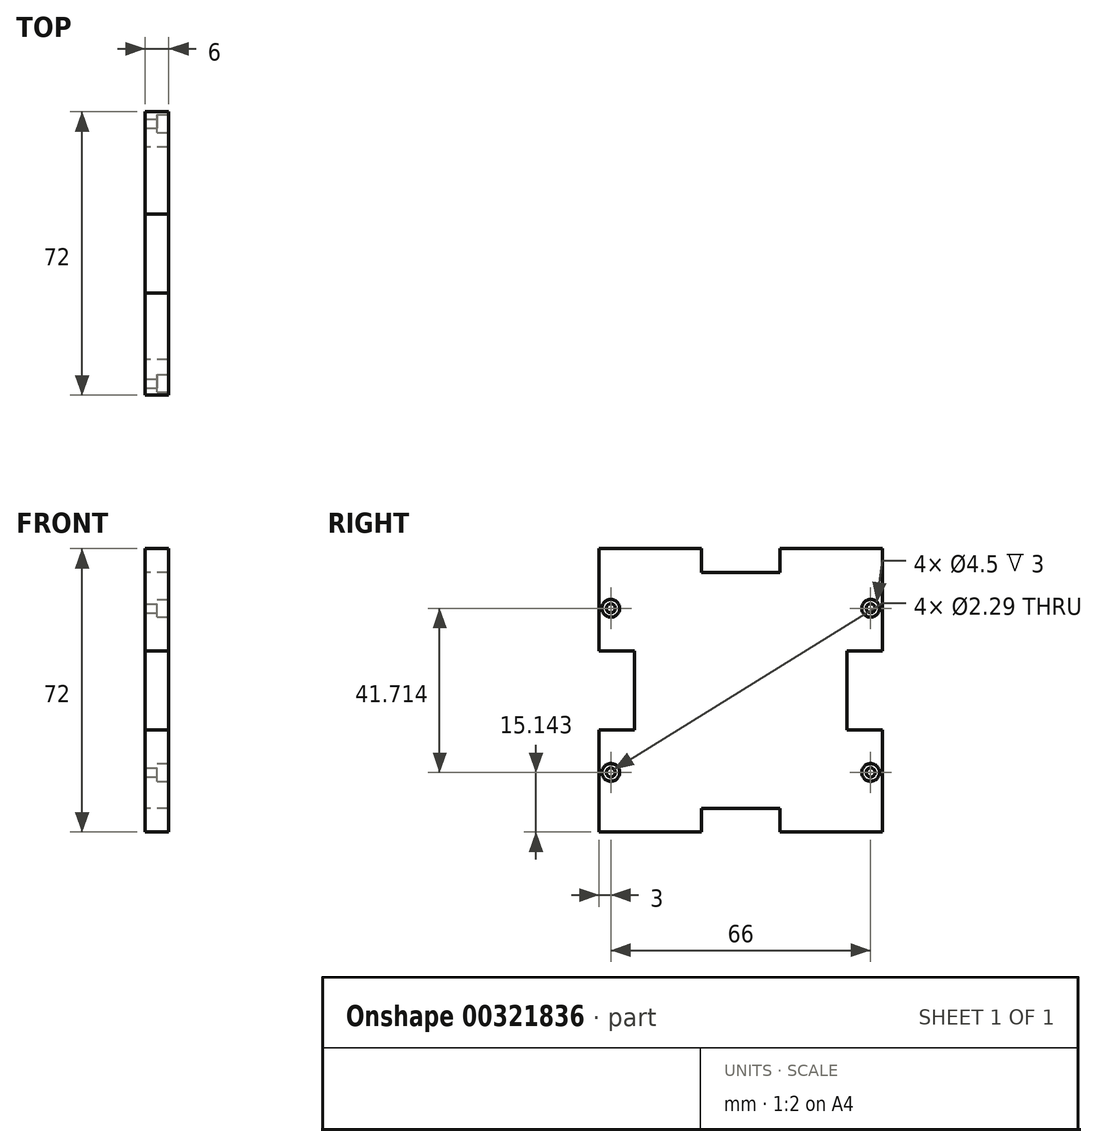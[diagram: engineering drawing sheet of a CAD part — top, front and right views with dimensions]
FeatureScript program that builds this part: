
annotation { "Feature Type Name" : "Feature", "Feature Type Description" : "" }
export const myFeature = defineFeature(function(context is Context, id is Id, definition is map)
    precondition{}
    {
        {
            var Q0;
            Q0=qCreatedBy(makeId("Right.planeOp"),FACE);
            var sketch = newSketch(context, id + "F0", { "sketchPlane" : qUnion([Q0])});
            skLineSegment(sketch, "E0.bottom", {"start": v(-36, -36) * mm, "end": v(36, -36) * mm});
            skLineSegment(sketch, "E0.top", {"start": v(-36, 36) * mm, "end": v(36, 36) * mm});
            skLineSegment(sketch, "E0.left", {"start": v(-36, -36) * mm, "end": v(-36, 36) * mm});
            skLineSegment(sketch, "E0.right", {"start": v(36, -36) * mm, "end": v(36, 36) * mm});
            skPoint(sketch, "E0.middle", {"position": v(0, 0) * mm});
            skLineSegment(sketch, "E1", {"start": v(0, 36) * mm, "end": v(0, -36) * mm, "construction": true});
            skLineSegment(sketch, "E2", {"start": v(-36, 0) * mm, "end": v(36, 0) * mm, "construction": true});
            skLineSegment(sketch, "E3", {"start": v(-36, 10) * mm, "end": v(-27, 10) * mm});
            skLineSegment(sketch, "E4", {"start": v(-27, 10) * mm, "end": v(-27, -10) * mm});
            skLineSegment(sketch, "E5", {"start": v(-27, -10) * mm, "end": v(-36, -10) * mm});
            skLineSegment(sketch, "E6.MirrorCS", {"start": v(36, 10) * mm, "end": v(27, 10) * mm});
            skLineSegment(sketch, "E7.MirrorCS", {"start": v(27, 10) * mm, "end": v(27, -10) * mm});
            skLineSegment(sketch, "E8.MirrorCS", {"start": v(27, -10) * mm, "end": v(36, -10) * mm});
            skLineSegment(sketch, "E9", {"start": v(-10, 36) * mm, "end": v(-10, 30) * mm});
            skLineSegment(sketch, "E10", {"start": v(-10, 30) * mm, "end": v(10, 30) * mm});
            skLineSegment(sketch, "E11", {"start": v(10, 30) * mm, "end": v(10, 36) * mm});
            skLineSegment(sketch, "E12.MirrorCS", {"start": v(10, -30) * mm, "end": v(10, -36) * mm});
            skLineSegment(sketch, "E13.MirrorCS", {"start": v(-10, -36) * mm, "end": v(-10, -30) * mm});
            skLineSegment(sketch, "E14.MirrorCS", {"start": v(0, -36) * mm, "end": v(0, 36) * mm, "construction": true});
            skLineSegment(sketch, "E15.MirrorCS", {"start": v(-10, -30) * mm, "end": v(10, -30) * mm});
            skSolve(sketch);
        }
        {
            var Q0;
            Q0 = qSketchRegion(id + "F0", true);
            extrude(context, id + "F1", {"entities" : qUnion([Q0]), "depth" : 6 * mm});
        }
        {
            var Q0;
            {var subQ0=sQuery(id+"F0.wireOp",EDGE,"E9");Q0=makeQuery(id+"F0.imprint","IMPRINT",FACE,{"disambiguationData":[TD([[makeQuery(id+"F0.imprint","IMPRINT",EDGE,{"derivedFrom":subQ0}),1.0]])]});}
            var Q1;
            {var subQ0=sQuery(id+"F0.wireOp",EDGE,"E6.MirrorCS");Q1=makeQuery(id+"F0.imprint","IMPRINT",FACE,{"disambiguationData":[TD([[makeQuery(id+"F0.imprint","IMPRINT",EDGE,{"derivedFrom":subQ0}),1.0]])]});}
            var Q2;
            {var subQ0=sQuery(id+"F0.wireOp",EDGE,"E12.MirrorCS");Q2=makeQuery(id+"F0.imprint","IMPRINT",FACE,{"disambiguationData":[TD([[makeQuery(id+"F0.imprint","IMPRINT",EDGE,{"derivedFrom":subQ0}),-1.0]])]});}
            var Q3;
            {var subQ0=sQuery(id+"F0.wireOp",EDGE,"E3");Q3=makeQuery(id+"F0.imprint","IMPRINT",FACE,{"disambiguationData":[TD([[makeQuery(id+"F0.imprint","IMPRINT",EDGE,{"derivedFrom":subQ0}),-1.0]])]});}
            extrude(context, id + "F2", {"entities" : qUnion([Q0, Q1, Q2, Q3]), "operationType" : NewBodyOperationType.REMOVE, "endBound" : BoundingType.UP_TO_NEXT, "depth" : 25 * mm});
        }
        {
            var Q0;
            Q0=makeQuery(id+"F1.opExtrude","CAP_FACE",FACE,{"disambiguationData":[OSD([sQuery(id+"F0.wireOp",EDGE,"E0.top"),sQuery(id+"F0.wireOp",EDGE,"E0.left"),sQuery(id+"F0.wireOp",EDGE,"E0.right"),sQuery(id+"F0.wireOp",EDGE,"E0.bottom")])],"isStart":false});
            var sketch = newSketch(context, id + "F3", { "sketchPlane" : qUnion([Q0])});
            skCircle(sketch, "E16", {"center": v(-33, 20.86) * mm, "radius": 2.25 * mm});
            skCircle(sketch, "E17.MirrorC", {"center": v(-33, -20.86) * mm, "radius": 2.25 * mm});
            skCircle(sketch, "E18.MirrorC", {"center": v(33, 20.86) * mm, "radius": 2.25 * mm});
            skCircle(sketch, "E19.MirrorC", {"center": v(33, -20.86) * mm, "radius": 2.25 * mm});
            skCircle(sketch, "E20", {"center": v(-33, 20.86) * mm, "radius": 1.14 * mm});
            skCircle(sketch, "E21.MirrorC", {"center": v(33, 20.86) * mm, "radius": 1.14 * mm});
            skCircle(sketch, "E22.MirrorC", {"center": v(33, -20.86) * mm, "radius": 1.14 * mm});
            skCircle(sketch, "E23.MirrorC", {"center": v(-33, -20.86) * mm, "radius": 1.14 * mm});
            skSolve(sketch);
        }
        {
            var Q0;
            Q0 = qSketchRegion(id + "F3", true);
            extrude(context, id + "F4", {"entities" : qUnion([Q0]), "operationType" : NewBodyOperationType.REMOVE, "oppositeDirection" : true, "depth" : 3 * mm});
        }
        {
            var Q0;
            Q0=makeQuery(id+"F4.boolean.opBoolean","SPLIT",FACE,{"disambiguationData":[TD([makeQuery(id+"F4.opExtrude","SWEPT_FACE",FACE,{"disambiguationData":[OSD([sQuery(id+"F3.wireOp",EDGE,"E20")])]})])],"derivedFrom":makeQuery(id+"F1.opExtrude","CAP_FACE",FACE,{"disambiguationData":[OSD([sQuery(id+"F0.wireOp",EDGE,"E0.top"),sQuery(id+"F0.wireOp",EDGE,"E0.left"),sQuery(id+"F0.wireOp",EDGE,"E0.right"),sQuery(id+"F0.wireOp",EDGE,"E0.bottom")])],"isStart":false})});
            var Q1;
            Q1=makeQuery(id+"F4.boolean.opBoolean","SPLIT",FACE,{"disambiguationData":[TD([makeQuery(id+"F4.opExtrude","SWEPT_FACE",FACE,{"disambiguationData":[OSD([sQuery(id+"F3.wireOp",EDGE,"E21.MirrorC")])]})])],"derivedFrom":makeQuery(id+"F1.opExtrude","CAP_FACE",FACE,{"disambiguationData":[OSD([sQuery(id+"F0.wireOp",EDGE,"E0.top"),sQuery(id+"F0.wireOp",EDGE,"E0.left"),sQuery(id+"F0.wireOp",EDGE,"E0.right"),sQuery(id+"F0.wireOp",EDGE,"E0.bottom")])],"isStart":false})});
            var Q2;
            Q2=makeQuery(id+"F4.boolean.opBoolean","SPLIT",FACE,{"disambiguationData":[TD([makeQuery(id+"F4.opExtrude","SWEPT_FACE",FACE,{"disambiguationData":[OSD([sQuery(id+"F3.wireOp",EDGE,"E22.MirrorC")])]})])],"derivedFrom":makeQuery(id+"F1.opExtrude","CAP_FACE",FACE,{"disambiguationData":[OSD([sQuery(id+"F0.wireOp",EDGE,"E0.top"),sQuery(id+"F0.wireOp",EDGE,"E0.left"),sQuery(id+"F0.wireOp",EDGE,"E0.right"),sQuery(id+"F0.wireOp",EDGE,"E0.bottom")])],"isStart":false})});
            var Q3;
            Q3=makeQuery(id+"F4.boolean.opBoolean","SPLIT",FACE,{"disambiguationData":[TD([makeQuery(id+"F4.opExtrude","SWEPT_FACE",FACE,{"disambiguationData":[OSD([sQuery(id+"F3.wireOp",EDGE,"E23.MirrorC")])]})])],"derivedFrom":makeQuery(id+"F1.opExtrude","CAP_FACE",FACE,{"disambiguationData":[OSD([sQuery(id+"F0.wireOp",EDGE,"E0.top"),sQuery(id+"F0.wireOp",EDGE,"E0.left"),sQuery(id+"F0.wireOp",EDGE,"E0.right"),sQuery(id+"F0.wireOp",EDGE,"E0.bottom")])],"isStart":false})});
            extrude(context, id + "F5", {"entities" : qUnion([Q0, Q1, Q2, Q3]), "operationType" : NewBodyOperationType.REMOVE, "endBound" : BoundingType.THROUGH_ALL, "oppositeDirection" : true, "depth" : 25 * mm});
        }
    });
